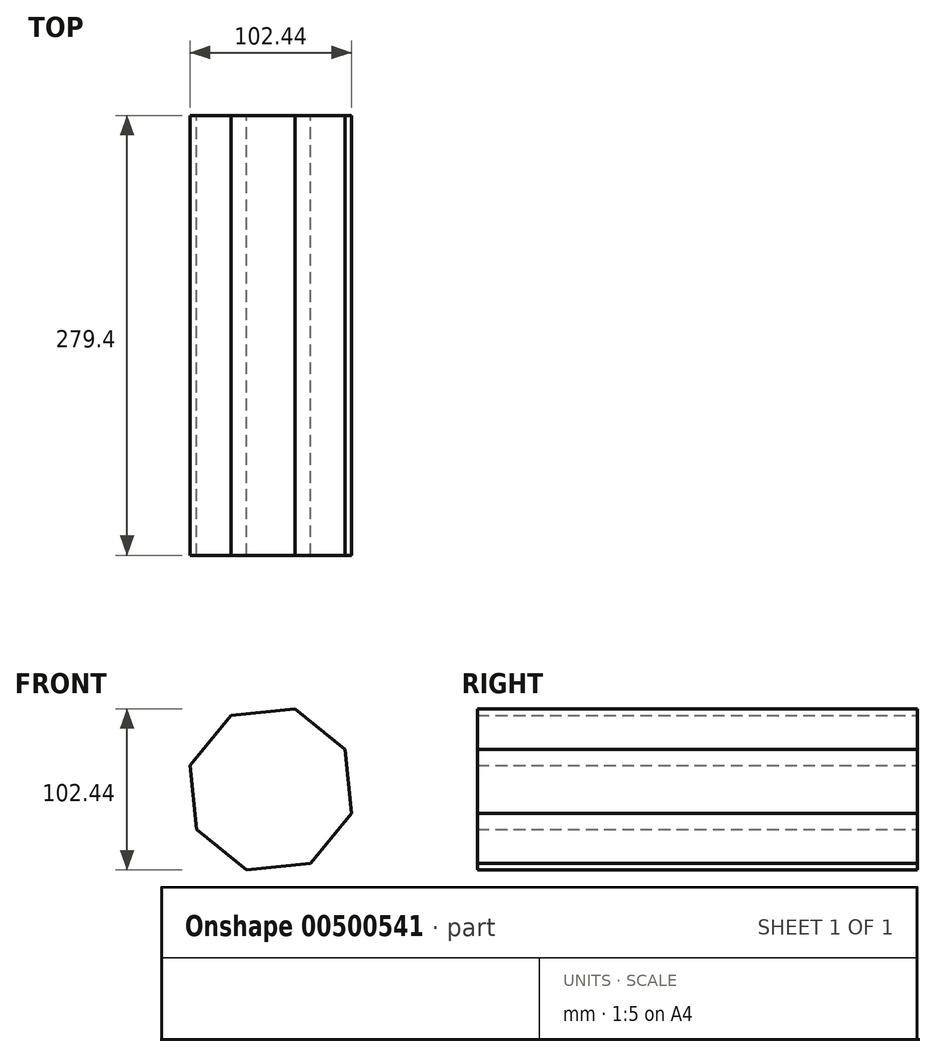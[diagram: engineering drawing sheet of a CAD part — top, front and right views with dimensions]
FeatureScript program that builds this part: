
annotation { "Feature Type Name" : "Feature", "Feature Type Description" : "" }
export const myFeature = defineFeature(function(context is Context, id is Id, definition is map)
    precondition{}
    {
        {
            var Q0;
            Q0=qCreatedBy(makeId("Front.planeOp"),FACE);
            var sketch = newSketch(context, id + "F0", { "sketchPlane" : qUnion([Q0])});
            skCircle(sketch, "E0.cCircle", {"center": v(0, 0) * mm, "radius": 53.47 * mm, "construction": true});
            skLineSegment(sketch, "E0.0", {"start": v(-25.36, 47.07) * mm, "end": v(15.35, 51.22) * mm});
            skLineSegment(sketch, "E0.1", {"start": v(15.35, 51.22) * mm, "end": v(47.07, 25.36) * mm});
            skLineSegment(sketch, "E0.2", {"start": v(47.07, 25.36) * mm, "end": v(51.22, -15.35) * mm});
            skLineSegment(sketch, "E0.3", {"start": v(51.22, -15.35) * mm, "end": v(25.36, -47.07) * mm});
            skLineSegment(sketch, "E0.4", {"start": v(25.36, -47.07) * mm, "end": v(-15.35, -51.22) * mm});
            skLineSegment(sketch, "E0.5", {"start": v(-15.35, -51.22) * mm, "end": v(-47.07, -25.36) * mm});
            skLineSegment(sketch, "E0.6", {"start": v(-47.07, -25.36) * mm, "end": v(-51.22, 15.35) * mm});
            skLineSegment(sketch, "E0.7", {"start": v(-51.22, 15.35) * mm, "end": v(-25.36, 47.07) * mm});
            skSolve(sketch);
        }
        {
            var Q0;
            Q0=makeQuery(id+"F0.imprint","IMPRINT",FACE,{"disambiguationData":[TD([[makeQuery(id+"F0.imprint","IMPRINT",EDGE,{"derivedFrom":sQuery(id+"F0.wireOp",EDGE,"E0.0")}),-1.0]])]});
            extrude(context, id + "F1", {"entities" : qUnion([Q0]), "depth" : 279.4 * mm});
        }
    });
